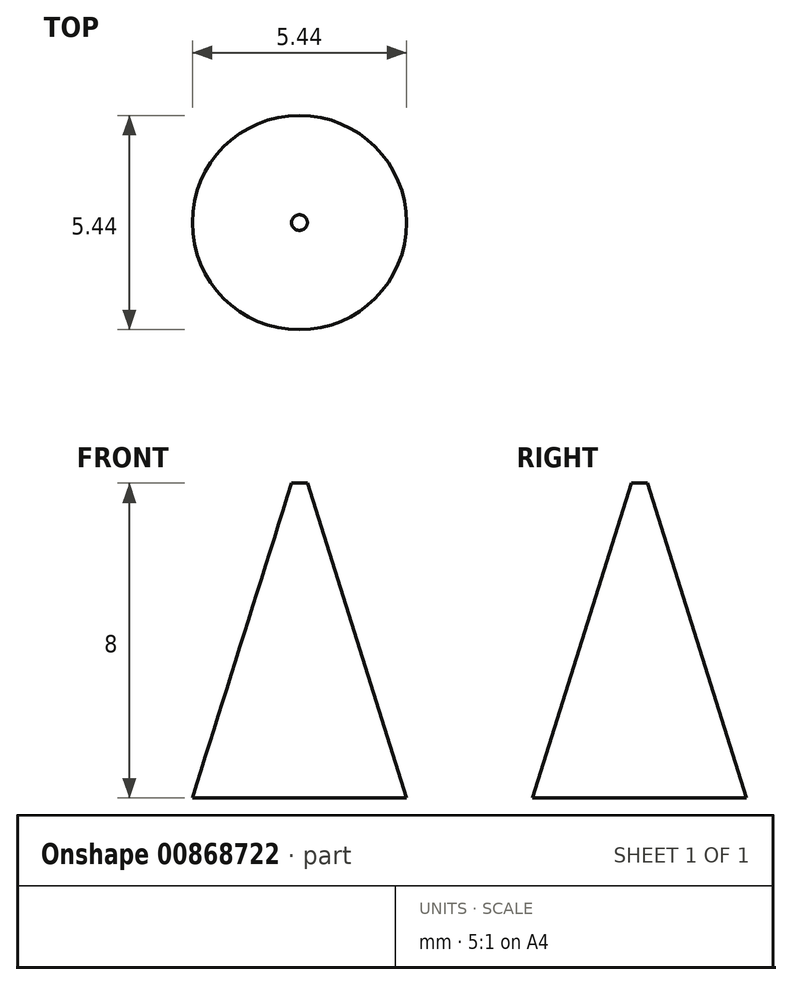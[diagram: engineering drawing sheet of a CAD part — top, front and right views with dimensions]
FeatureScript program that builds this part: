
annotation { "Feature Type Name" : "Feature", "Feature Type Description" : "" }
export const myFeature = defineFeature(function(context is Context, id is Id, definition is map)
    precondition{}
    {
        {
            var Q0;
            Q0=qCreatedBy(makeId("Front.planeOp"),FACE);
            var sketch = newSketch(context, id + "F0", { "sketchPlane" : qUnion([Q0])});
            skLineSegment(sketch, "E0", {"start": v(0, 0) * mm, "end": v(-0.2, 0) * mm});
            skLineSegment(sketch, "E1", {"start": v(-0.2, 0) * mm, "end": v(-2.72, -8) * mm});
            skLineSegment(sketch, "E2", {"start": v(-2.72, -8) * mm, "end": v(0, -8) * mm});
            skLineSegment(sketch, "E3", {"start": v(0, -8) * mm, "end": v(0, 0) * mm});
            skSolve(sketch);
        }
        {
            var Q0;
            Q0=makeQuery(id+"F0.imprint","IMPRINT",FACE,{"disambiguationData":[TD([[makeQuery(id+"F0.imprint","IMPRINT",EDGE,{"derivedFrom":sQuery(id+"F0.wireOp",EDGE,"E0")}),1.0]])]});
            var Q1;
            Q1=sQuery(id+"F0.wireOp",EDGE,"E3");
            revolve(context, id + "F1", {"surfaceOperationType" : NewSurfaceOperationType.NEW, "entities" : qUnion([Q0]), "axis" : qUnion([Q1]), "revolveType" : RevolveType.FULL});
        }
    });
